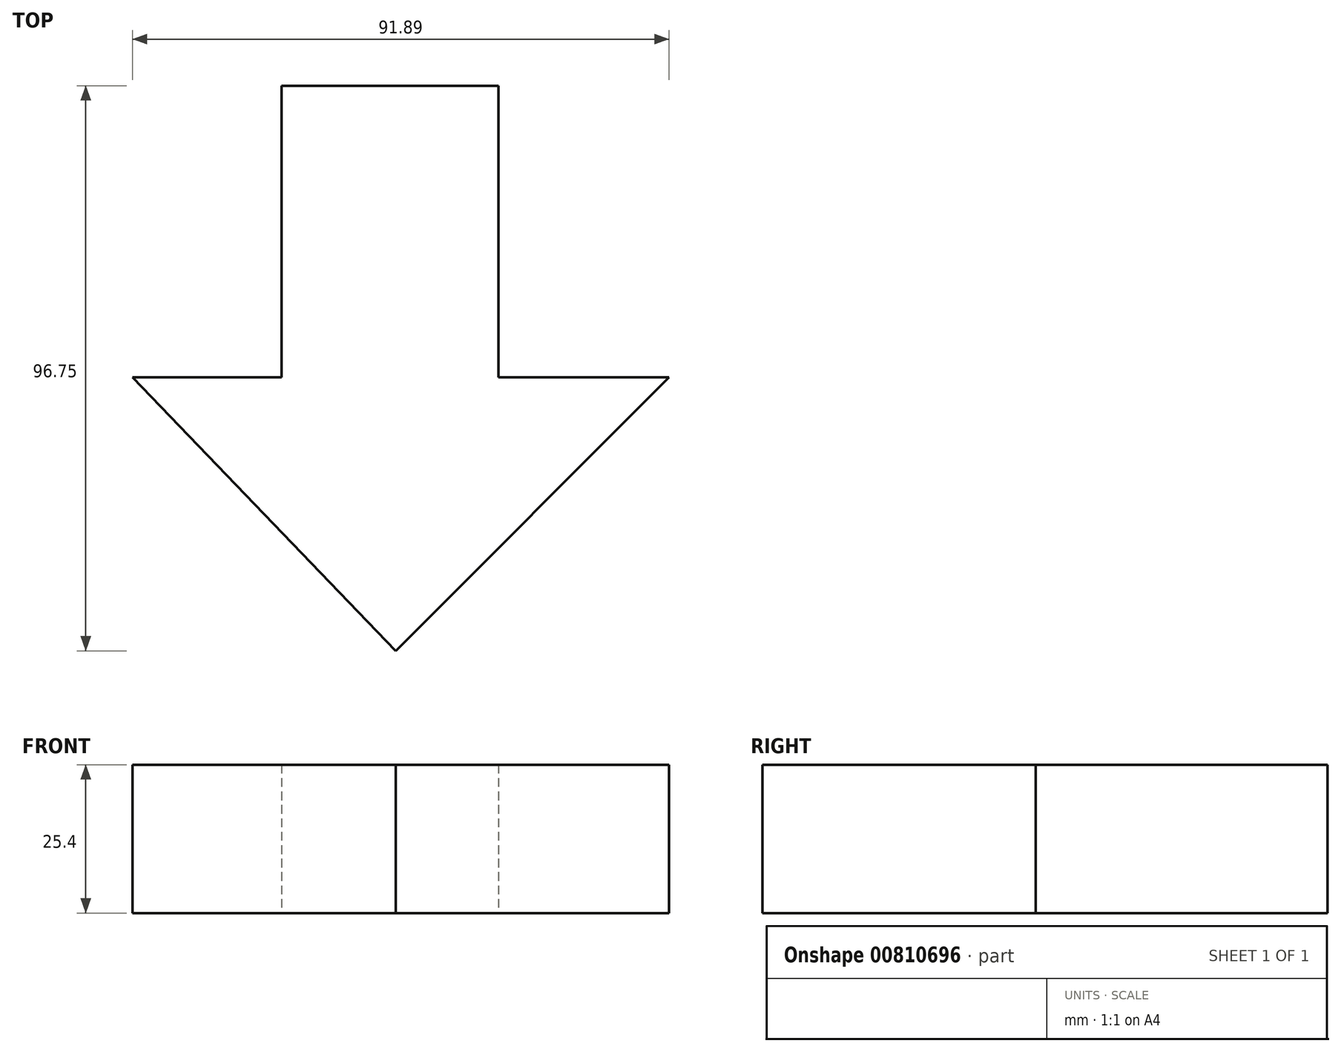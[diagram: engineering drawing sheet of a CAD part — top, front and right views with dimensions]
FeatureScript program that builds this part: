
annotation { "Feature Type Name" : "Feature", "Feature Type Description" : "" }
export const myFeature = defineFeature(function(context is Context, id is Id, definition is map)
    precondition{}
    {
        {
            var Q0;
            Q0=qCreatedBy(makeId("Top.planeOp"),FACE);
            var sketch = newSketch(context, id + "F0", { "sketchPlane" : qUnion([Q0])});
            skLineSegment(sketch, "E0", {"start": v(0, 49.93) * mm, "end": v(-19.56, 49.93) * mm});
            skLineSegment(sketch, "E1", {"start": v(-19.56, 49.93) * mm, "end": v(-19.56, 0) * mm});
            skLineSegment(sketch, "E2", {"start": v(0, 49.93) * mm, "end": v(17.62, 49.93) * mm});
            skLineSegment(sketch, "E3", {"start": v(17.62, 49.93) * mm, "end": v(17.62, 0) * mm});
            skLineSegment(sketch, "E4", {"start": v(17.62, 0) * mm, "end": v(46.82, 0) * mm});
            skLineSegment(sketch, "E5", {"start": v(-19.56, 0) * mm, "end": v(-45.07, 0) * mm});
            skLineSegment(sketch, "E6", {"start": v(-45.07, 0) * mm, "end": v(0, -46.82) * mm});
            skLineSegment(sketch, "E7", {"start": v(46.82, 0) * mm, "end": v(0, -46.82) * mm});
            skSolve(sketch);
        }
        {
            var Q0;
            Q0=makeQuery(id+"F0.imprint","IMPRINT",FACE,{"disambiguationData":[TD([[makeQuery(id+"F0.imprint","IMPRINT",EDGE,{"derivedFrom":sQuery(id+"F0.wireOp",EDGE,"E0")}),1.0]])]});
            extrude(context, id + "F1", {"entities" : qUnion([Q0]), "depth" : 25.4 * mm, "offsetDistance" : 25.4 * mm});
        }
    });
